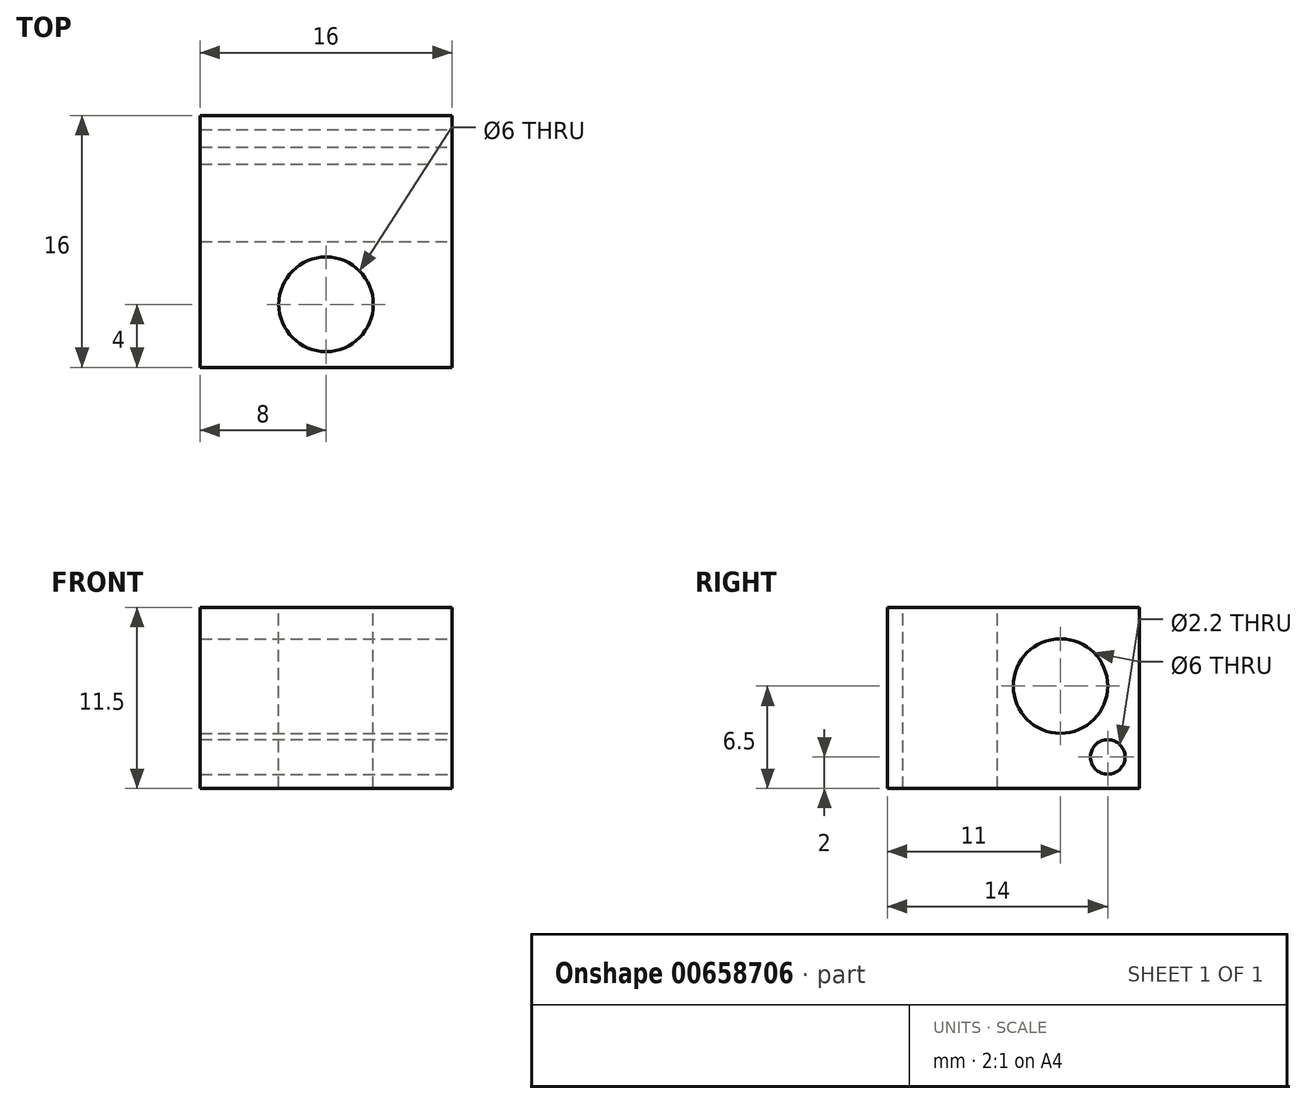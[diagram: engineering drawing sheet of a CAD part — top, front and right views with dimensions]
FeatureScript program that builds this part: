
annotation { "Feature Type Name" : "Feature", "Feature Type Description" : "" }
export const myFeature = defineFeature(function(context is Context, id is Id, definition is map)
    precondition{}
    {
        {
            var Q0;
            Q0=qCreatedBy(makeId("Top.planeOp"),FACE);
            var sketch = newSketch(context, id + "F0", { "sketchPlane" : qUnion([Q0])});
            skLineSegment(sketch, "E0.rect.bottom", {"start": v(8, -8) * mm, "end": v(-8, -8) * mm});
            skLineSegment(sketch, "E0.rect.top", {"start": v(8, 8) * mm, "end": v(-8, 8) * mm});
            skLineSegment(sketch, "E0.rect.left", {"start": v(8, -8) * mm, "end": v(8, 8) * mm});
            skLineSegment(sketch, "E0.rect.right", {"start": v(-8, -8) * mm, "end": v(-8, 8) * mm});
            skPoint(sketch, "E0.rect.middle", {"position": v(0, 0) * mm});
            skSolve(sketch);
        }
        {
            var Q0;
            Q0=makeQuery(id+"F0.imprint","IMPRINT",FACE,{"disambiguationData":[TD([[makeQuery(id+"F0.imprint","IMPRINT",EDGE,{"derivedFrom":sQuery(id+"F0.wireOp",EDGE,"E0.rect.bottom")}),-1.0]])]});
            extrude(context, id + "F1", {"entities" : qUnion([Q0]), "depth" : 11.5 * mm});
        }
        {
            var Q0;
            Q0=makeQuery(id+"F1.opExtrude","CAP_FACE",FACE,{"disambiguationData":[OSD([sQuery(id+"F0.wireOp",EDGE,"E0.rect.bottom"),sQuery(id+"F0.wireOp",EDGE,"E0.rect.top"),sQuery(id+"F0.wireOp",EDGE,"E0.rect.left"),sQuery(id+"F0.wireOp",EDGE,"E0.rect.right")])],"isStart":false});
            var sketch = newSketch(context, id + "F2", { "sketchPlane" : qUnion([Q0])});
            skCircle(sketch, "E1", {"center": v(0, -4) * mm, "radius": 3 * mm});
            skSolve(sketch);
        }
        {
            var Q0;
            Q0=makeQuery(id+"F2.imprint","IMPRINT",FACE,{"disambiguationData":[TD([[makeQuery(id+"F2.imprint","IMPRINT",EDGE,{"derivedFrom":sQuery(id+"F2.wireOp",EDGE,"E1")}),1.0]])]});
            extrude(context, id + "F3", {"entities" : qUnion([Q0]), "operationType" : NewBodyOperationType.REMOVE, "oppositeDirection" : true, "depth" : 25 * mm});
        }
        {
            var Q0;
            Q0=makeQuery(id+"F1.opExtrude","SWEPT_FACE",FACE,{"disambiguationData":[OSD([sQuery(id+"F0.wireOp",EDGE,"E0.rect.left")])]});
            var sketch = newSketch(context, id + "F4", { "sketchPlane" : qUnion([Q0])});
            skCircle(sketch, "E2", {"center": v(3, 6.5) * mm, "radius": 3 * mm});
            skCircle(sketch, "E3", {"center": v(6, 2) * mm, "radius": 1.1 * mm});
            skSolve(sketch);
        }
        {
            var Q0;
            Q0=makeQuery(id+"F4.imprint","IMPRINT",FACE,{"disambiguationData":[TD([[makeQuery(id+"F4.imprint","IMPRINT",EDGE,{"derivedFrom":sQuery(id+"F4.wireOp",EDGE,"E2")}),1.0]])]});
            var Q1;
            Q1=makeQuery(id+"F4.imprint","IMPRINT",FACE,{"disambiguationData":[TD([[makeQuery(id+"F4.imprint","IMPRINT",EDGE,{"derivedFrom":sQuery(id+"F4.wireOp",EDGE,"E3")}),1.0]])]});
            extrude(context, id + "F5", {"entities" : qUnion([Q0, Q1]), "operationType" : NewBodyOperationType.REMOVE, "endBound" : BoundingType.THROUGH_ALL, "oppositeDirection" : true, "depth" : 25 * mm});
        }
    });
